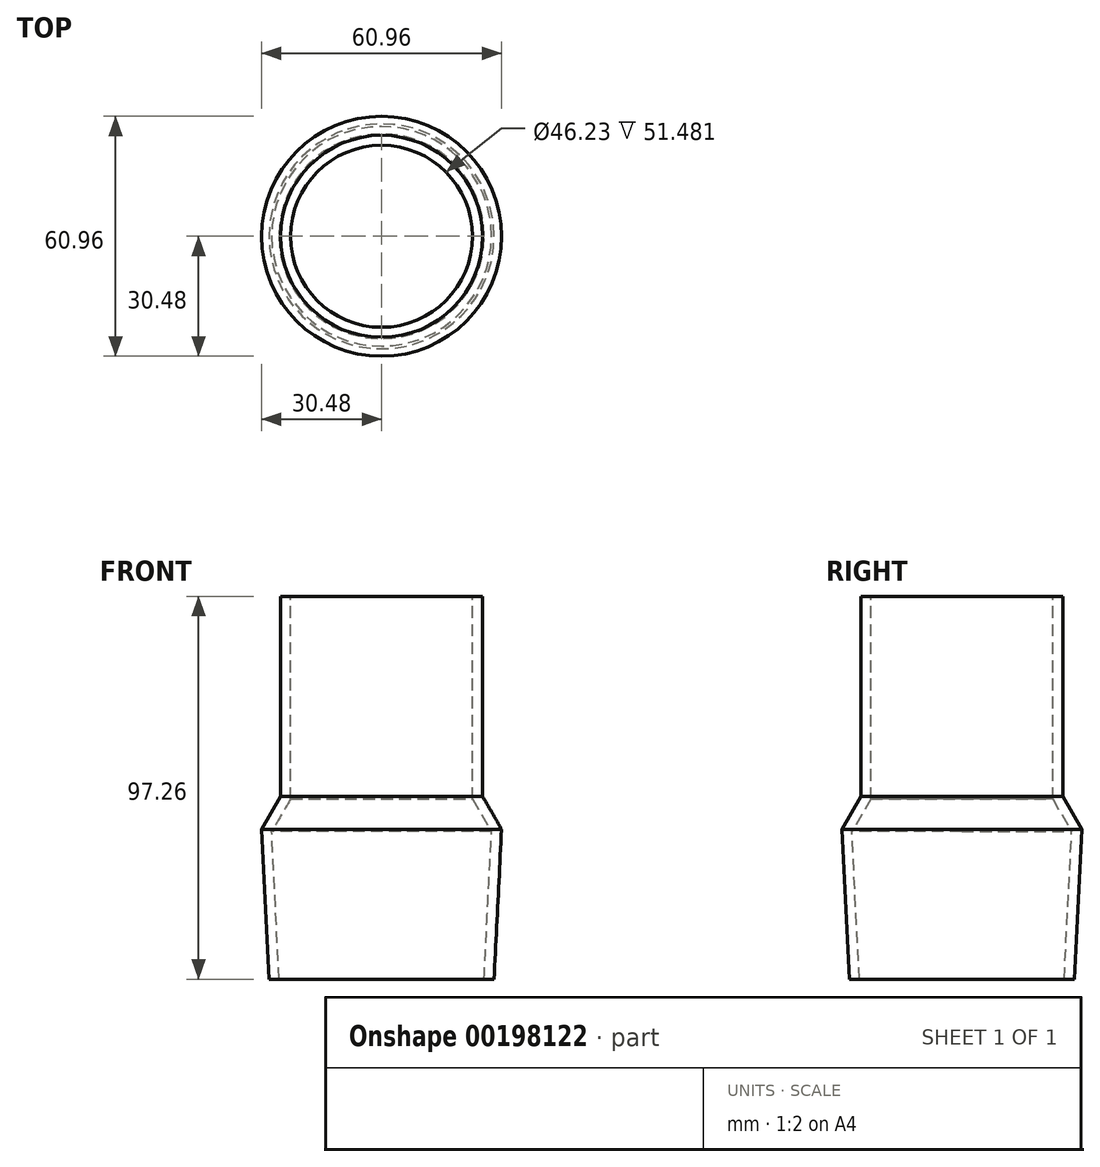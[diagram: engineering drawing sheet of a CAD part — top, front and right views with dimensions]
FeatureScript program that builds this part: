
annotation { "Feature Type Name" : "Feature", "Feature Type Description" : "" }
export const myFeature = defineFeature(function(context is Context, id is Id, definition is map)
    precondition{}
    {
        {
            var Q0;
            Q0=qCreatedBy(makeId("Front.planeOp"),FACE);
            var sketch = newSketch(context, id + "F0", { "sketchPlane" : qUnion([Q0])});
            skLineSegment(sketch, "E0", {"start": v(-28.58, -73.92) * mm, "end": v(-30.48, -35.82) * mm});
            skLineSegment(sketch, "E1", {"start": v(-30.48, -35.82) * mm, "end": v(-25.65, -27.46) * mm});
            skLineSegment(sketch, "E2", {"start": v(-25.65, -27.46) * mm, "end": v(-25.65, 23.34) * mm});
            skLineSegment(sketch, "E3", {"start": v(-25.65, 23.34) * mm, "end": v(0, 23.34) * mm});
            skLineSegment(sketch, "E4", {"start": v(0, 23.34) * mm, "end": v(0, -73.92) * mm});
            skLineSegment(sketch, "E5", {"start": v(-28.57, -73.92) * mm, "end": v(0, -73.92) * mm});
            skSolve(sketch);
        }
        {
            var Q0;
            Q0=makeQuery(id+"F0.imprint","IMPRINT",FACE,{"disambiguationData":[TD([[makeQuery(id+"F0.imprint","IMPRINT",EDGE,{"derivedFrom":sQuery(id+"F0.wireOp",EDGE,"E0")}),-1.0]])]});
            var Q1;
            Q1=sQuery(id+"F0.wireOp",EDGE,"E4");
            revolve(context, id + "F1", {"entities" : qUnion([Q0]), "axis" : qUnion([Q1]), "revolveType" : RevolveType.FULL});
        }
        {
            var Q0;
            Q0=makeQuery(id+"F1.opRevolve","SWEPT_FACE",FACE,{"disambiguationData":[OSD([sQuery(id+"F0.wireOp",EDGE,"E3")])]});
            var Q1;
            Q1=makeQuery(id+"F1.opRevolve","SWEPT_FACE",FACE,{"disambiguationData":[OSD([sQuery(id+"F0.wireOp",EDGE,"E5")])]});
            shell(context, id + "F2", {"entities" : qUnion([Q0, Q1]), "thickness" : 2.54 * mm});
        }
    });
